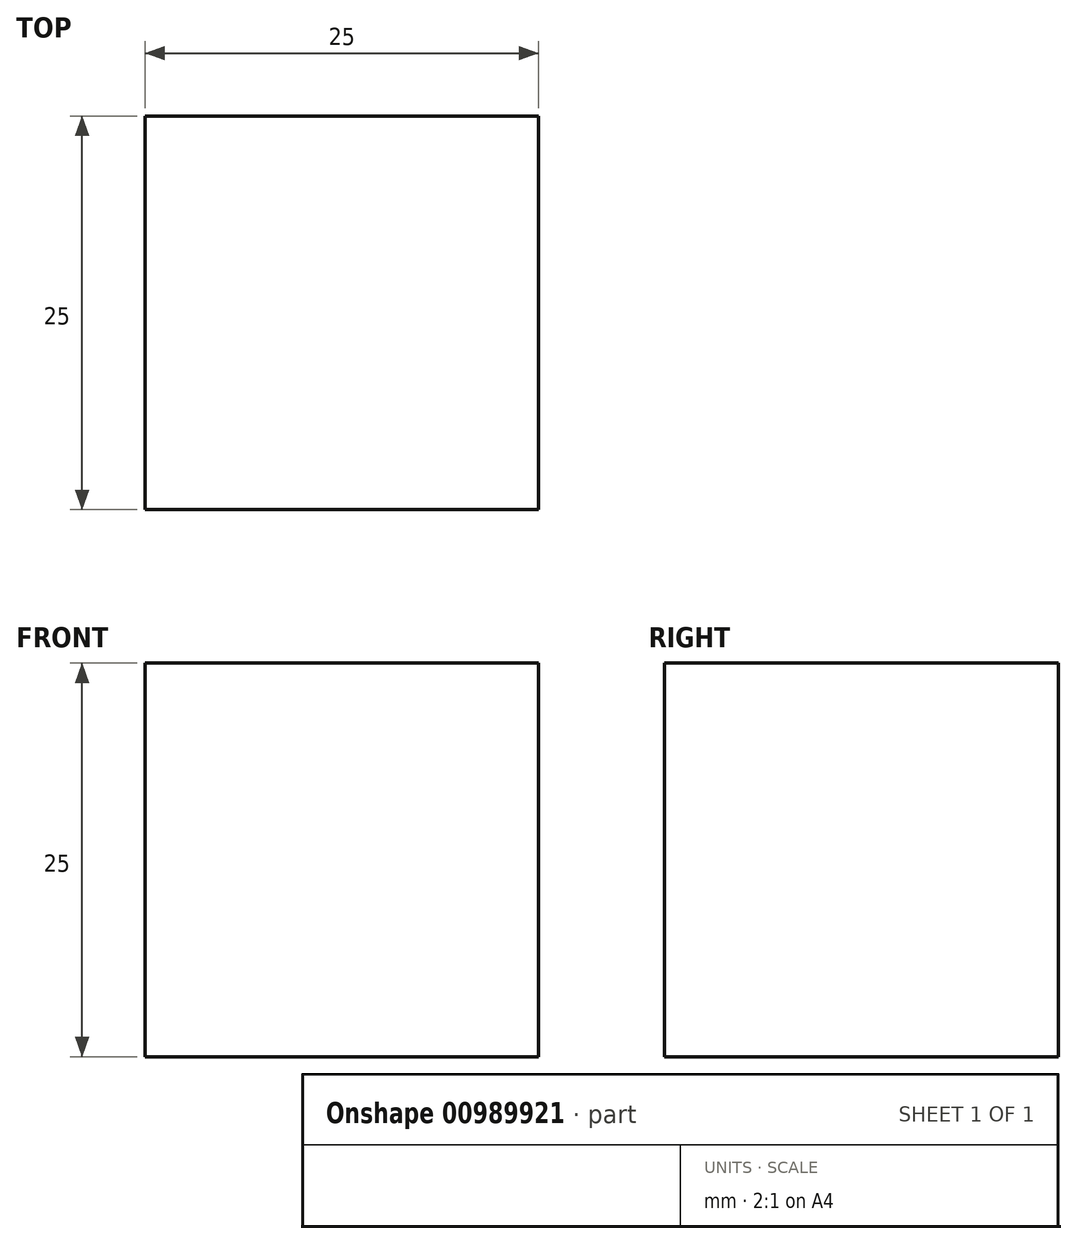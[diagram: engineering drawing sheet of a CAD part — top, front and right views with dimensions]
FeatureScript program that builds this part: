
annotation { "Feature Type Name" : "Feature", "Feature Type Description" : "" }
export const myFeature = defineFeature(function(context is Context, id is Id, definition is map)
    precondition{}
    {
        {
            var Q0;
            Q0=qCreatedBy(makeId("Top.planeOp"),FACE);
            var sketch = newSketch(context, id + "F0", { "sketchPlane" : qUnion([Q0])});
            skLineSegment(sketch, "E0.bottom", {"start": v(12.5, -12.5) * mm, "end": v(-12.5, -12.5) * mm});
            skLineSegment(sketch, "E0.top", {"start": v(12.5, 12.5) * mm, "end": v(-12.5, 12.5) * mm});
            skLineSegment(sketch, "E0.left", {"start": v(12.5, -12.5) * mm, "end": v(12.5, 12.5) * mm});
            skLineSegment(sketch, "E0.right", {"start": v(-12.5, -12.5) * mm, "end": v(-12.5, 12.5) * mm});
            skPoint(sketch, "E0.middle", {"position": v(0, 0) * mm});
            skSolve(sketch);
        }
        {
            var Q0;
            Q0 = qSketchRegion(id + "F0", true);
            extrude(context, id + "F1", {"entities" : qUnion([Q0]), "flatOperationType" : FlatOperationType.REMOVE, "depth" : 25 * mm, "offsetDistance" : 25.4 * mm, "domain" : OperationDomain.MODEL});
        }
    });
